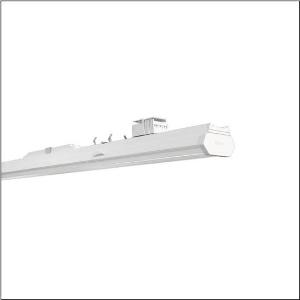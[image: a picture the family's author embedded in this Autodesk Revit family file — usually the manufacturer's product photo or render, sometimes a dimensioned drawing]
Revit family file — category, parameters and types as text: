
# Revit family: licross_r__11_protected_extreme_ho_51tp12dn4fxme_36ff
name_source: partatom
category: Lighting Fixtures
units: mm (PartAtom-declared; Revit-internal decimal feet)

## family parameters
Cut with Voids When Loaded = No
Host = Face
Light Source = No
Part Type = Normal
Room Calculation Point = No
Round Connector Dimension = Use Diameter
Shared = No

## types (1)
- --- (1 x LED, 15270 lm, 87.3 W, 4000K)
    Apparent Load = 87 VA
    CIE Flux Codes = 70 91 97 98 100
    Color Rendering = 80
    Color Temperature = 4000K
    Default Elevation = 1800 mm
    Description = Licross® 11 Protected extreme HO, luminaire insert, of sheet steel, galvanised, coil coated, white, length: 1.500mm, width: 90mm, height: 101mm, LED rated luminous flux: 15.270lm, light colour: 840, control gear: DALI 2, with plug, 5-pole, with phase selection, mains connection: 220..240V, AC, 50/60Hz, rated input power: 87W, halogen-free wiring, primary optical cover: cover, of PMMA, light emission: direct distribution, primary light characteristic: symmetric, protection rating (complete): IP64, insulation class (complete): insulation class I (protective earthing), certification: CE, ENEC, VDE, UKCA, protection symbol: D if used in an environment with conductive dust loads with corresponding accessories, impact resistance: IK06, permissible ambient temperature for indoor applications: -40..+40°C, corresponds to IFS (International Featured Standards) requirements for safety and quality in the food industry, reducing of maximum allowable ambient temperature of 5°C with ceiling mounting, LABS conformity tested according to VDMA 24364:2018-05, packaging unit: 1 piece
    Height = 92 mm
    Lamp = 1 x LED
    Lamp Light Flux = 15270 lm
    Lamp Power = 87.3 W
    Lamp count = 1
    Length = 1500 mm
    Luminous efficacy = 175 lm/W
    Manufacturer = Siteco
    ModVariant = No
    Model = 51TP12DN4FXME
    Mounting Place = Ceiling
    Mounting Type = Pendant
    Number of Poles = 1
    OnlyDefault = Yes
    Power Factor = 1
    Product Name = Licross® 11 Protected extreme HO
    Product group = luminaire insert
    ProductGroupID = 901
    Protection Class = Protection class I
    Protection Degree = IP 64
    RLX_Detail_Level = 1
    RLX_Emergency_Light_Flux = 0 lm
    RLX_Emergency_Type = 0
    RLX_Emergency_Type_DB = No
    RlxData = <blob elided: 24357 chars, md5=4afa9121>
    Socket = socket
    Standby Power = 0 W
    System Light Flux = 15270 lm
    System Power = 87 W
    Type Comments = factory setting: luminous flux: 100 % | dim-lin: 254 | 589 mA
    Type Image = l_1256148.jpg
    URL = http://relux.com
    VarID = @adj_052021
    Voltage = 0 V
    Weight = 0.00 kg
    Width = 88 mm

## geometry (parser evidence)
native form markers: Blend x4, Sweep x12
no freeform markers — native parametric forms only
